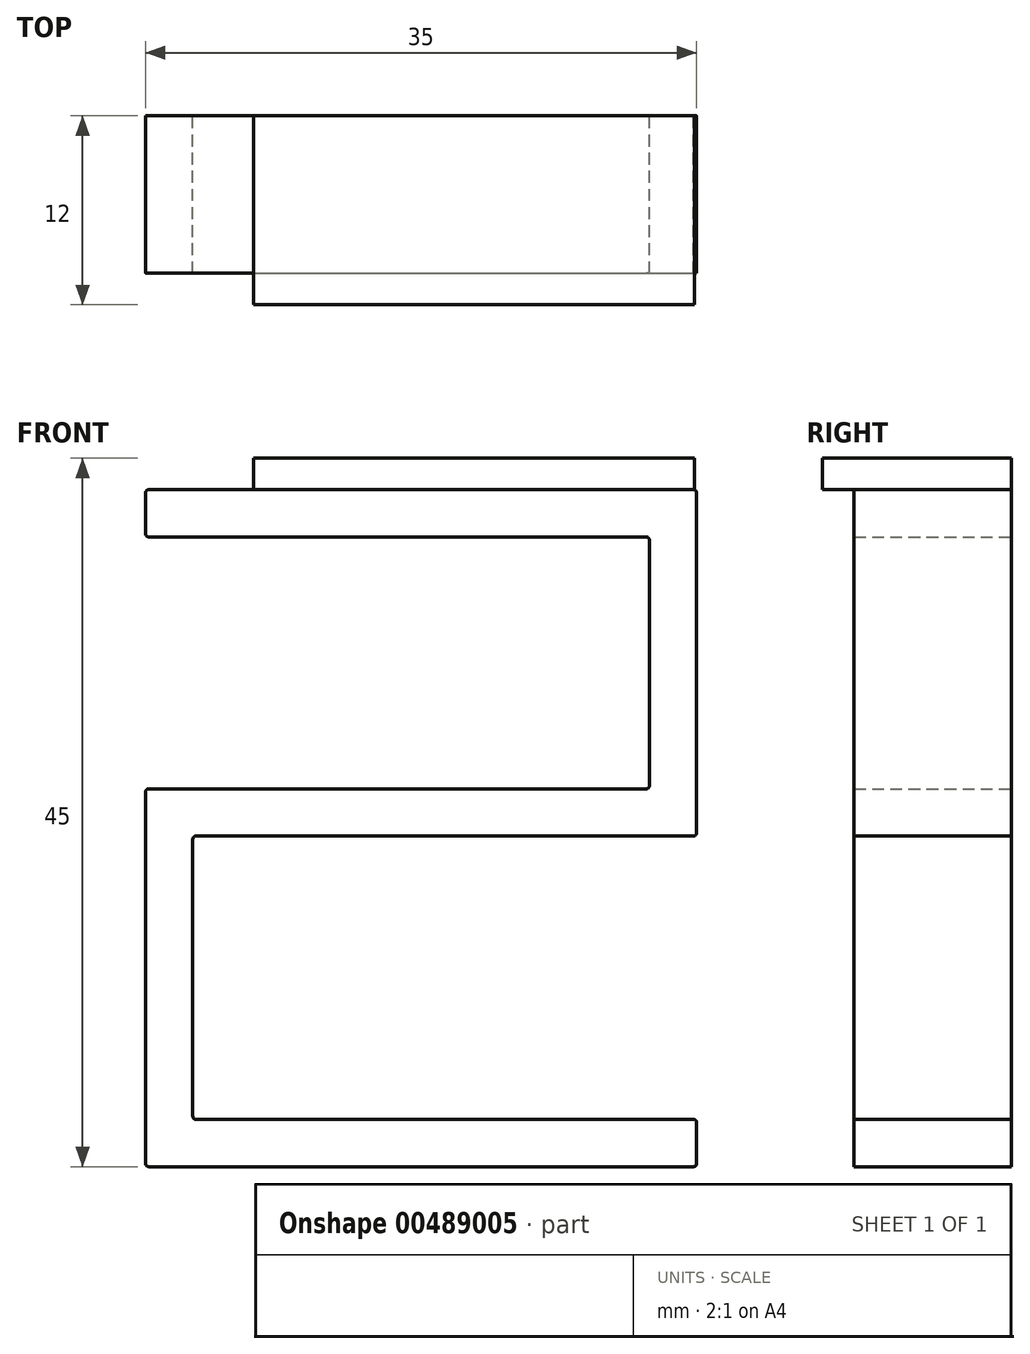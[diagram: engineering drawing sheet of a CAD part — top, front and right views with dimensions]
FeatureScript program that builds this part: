
annotation { "Feature Type Name" : "Feature", "Feature Type Description" : "" }
export const myFeature = defineFeature(function(context is Context, id is Id, definition is map)
    precondition{}
    {
        {
            var Q0;
            Q0=qCreatedBy(makeId("Front.planeOp"),FACE);
            var sketch = newSketch(context, id + "F0", { "sketchPlane" : qUnion([Q0])});
            skLineSegment(sketch, "E0.bottom", {"start": v(0, 0) * mm, "end": v(35, 0) * mm});
            skLineSegment(sketch, "E0.top", {"start": v(0, -43) * mm, "end": v(35, -43) * mm});
            skLineSegment(sketch, "E0.left", {"start": v(0, 0) * mm, "end": v(0, -3) * mm});
            skLineSegment(sketch, "E0.right", {"start": v(35, 0) * mm, "end": v(35, -22) * mm});
            skLineSegment(sketch, "E1.0", {"start": v(3, -40) * mm, "end": v(35, -40) * mm});
            skLineSegment(sketch, "E2.0", {"start": v(3, -22) * mm, "end": v(35, -22) * mm});
            skLineSegment(sketch, "E3.0", {"start": v(0, -19) * mm, "end": v(32, -19) * mm});
            skLineSegment(sketch, "E4.0", {"start": v(0, -3) * mm, "end": v(32, -3) * mm});
            skLineSegment(sketch, "E5.trimOffspring", {"start": v(3, -22) * mm, "end": v(3, -40) * mm});
            skLineSegment(sketch, "E6.trimOffspring", {"start": v(0, -19) * mm, "end": v(0, -43) * mm});
            skLineSegment(sketch, "E7.trimOffspring", {"start": v(32, -19) * mm, "end": v(32, -3) * mm});
            skLineSegment(sketch, "E8.trimOffspring", {"start": v(35, -40) * mm, "end": v(35, -43) * mm});
            skPoint(sketch, "E9.orphan", {"position": v(32, 0) * mm});
            skSolve(sketch);
        }
        {
            var Q0;
            Q0=makeQuery(id+"F0.imprint","IMPRINT",FACE,{"disambiguationData":[TD([[makeQuery(id+"F0.imprint","IMPRINT",EDGE,{"derivedFrom":sQuery(id+"F0.wireOp",EDGE,"E0.bottom")}),-1.0]])]});
            extrude(context, id + "F1", {"entities" : qUnion([Q0]), "depth" : 10 * mm, "offsetDistance" : 25 * mm});
        }
        {
            var Q0;
            Q0=makeQuery(id+"F1.opExtrude","SWEPT_EDGE",EDGE,{"disambiguationData":[OSD([sQuery(id+"F0.wireOp",EDGE,"E0.bottom"),sQuery(id+"F0.wireOp",EDGE,"E0.right")])]});
            var Q1;
            Q1=makeQuery(id+"F1.opExtrude","SWEPT_EDGE",EDGE,{"disambiguationData":[OSD([sQuery(id+"F0.wireOp",EDGE,"E4.0"),sQuery(id+"F0.wireOp",EDGE,"E7.trimOffspring")])]});
            var Q2;
            Q2=makeQuery(id+"F1.opExtrude","SWEPT_EDGE",EDGE,{"disambiguationData":[OSD([sQuery(id+"F0.wireOp",EDGE,"E0.right"),sQuery(id+"F0.wireOp",EDGE,"E2.0")])]});
            var Q3;
            Q3=makeQuery(id+"F1.opExtrude","SWEPT_EDGE",EDGE,{"disambiguationData":[OSD([sQuery(id+"F0.wireOp",EDGE,"E3.0"),sQuery(id+"F0.wireOp",EDGE,"E7.trimOffspring")])]});
            fillet(context, id + "F2", {"entities" : qUnion([Q0, Q1, Q2, Q3]), "radius" : 0.2 * mm, "tangentPropagation" : true, "allowEdgeOverflow" : false});
        }
        {
            var Q0;
            Q0=makeQuery(id+"F1.opExtrude","SWEPT_EDGE",EDGE,{"disambiguationData":[OSD([sQuery(id+"F0.wireOp",EDGE,"E1.0"),sQuery(id+"F0.wireOp",EDGE,"E5.trimOffspring")])]});
            var Q1;
            Q1=makeQuery(id+"F1.opExtrude","SWEPT_EDGE",EDGE,{"disambiguationData":[OSD([sQuery(id+"F0.wireOp",EDGE,"E1.0"),sQuery(id+"F0.wireOp",EDGE,"E8.trimOffspring")])]});
            var Q2;
            Q2=makeQuery(id+"F1.opExtrude","SWEPT_EDGE",EDGE,{"disambiguationData":[OSD([sQuery(id+"F0.wireOp",EDGE,"E0.top"),sQuery(id+"F0.wireOp",EDGE,"E8.trimOffspring")])]});
            var Q3;
            Q3=makeQuery(id+"F1.opExtrude","SWEPT_EDGE",EDGE,{"disambiguationData":[OSD([sQuery(id+"F0.wireOp",EDGE,"E0.top"),sQuery(id+"F0.wireOp",EDGE,"E6.trimOffspring")])]});
            var Q4;
            Q4=makeQuery(id+"F1.opExtrude","SWEPT_EDGE",EDGE,{"disambiguationData":[OSD([sQuery(id+"F0.wireOp",EDGE,"E2.0"),sQuery(id+"F0.wireOp",EDGE,"E5.trimOffspring")])]});
            var Q5;
            Q5=makeQuery(id+"F1.opExtrude","SWEPT_EDGE",EDGE,{"disambiguationData":[OSD([sQuery(id+"F0.wireOp",EDGE,"E3.0"),sQuery(id+"F0.wireOp",EDGE,"E6.trimOffspring")])]});
            var Q6;
            Q6=makeQuery(id+"F1.opExtrude","SWEPT_EDGE",EDGE,{"disambiguationData":[OSD([sQuery(id+"F0.wireOp",EDGE,"E0.bottom"),sQuery(id+"F0.wireOp",EDGE,"E0.left")])]});
            var Q7;
            Q7=makeQuery(id+"F1.opExtrude","SWEPT_EDGE",EDGE,{"disambiguationData":[OSD([sQuery(id+"F0.wireOp",EDGE,"E0.left"),sQuery(id+"F0.wireOp",EDGE,"E4.0")])]});
            fillet(context, id + "F3", {"entities" : qUnion([Q0, Q1, Q2, Q3, Q4, Q5, Q6, Q7]), "radius" : 0.2 * mm, "tangentPropagation" : true, "allowEdgeOverflow" : false});
        }
        {
            var Q0;
            Q0=qCreatedBy(makeId("Front.planeOp"),FACE);
            var sketch = newSketch(context, id + "F4", { "sketchPlane" : qUnion([Q0])});
            skLineSegment(sketch, "E10.bottom", {"start": v(34.86, 0) * mm, "end": v(6.86, 0) * mm});
            skLineSegment(sketch, "E10.top", {"start": v(34.86, 2) * mm, "end": v(6.86, 2) * mm});
            skLineSegment(sketch, "E10.left", {"start": v(34.86, 0) * mm, "end": v(34.86, 2) * mm});
            skLineSegment(sketch, "E10.right", {"start": v(6.86, 0) * mm, "end": v(6.86, 2) * mm});
            skSolve(sketch);
        }
        {
            var Q0;
            Q0=makeQuery(id+"F4.imprint","IMPRINT",FACE,{"disambiguationData":[TD([[makeQuery(id+"F4.imprint","IMPRINT",EDGE,{"derivedFrom":sQuery(id+"F4.wireOp",EDGE,"E10.bottom")}),-1.0]])]});
            extrude(context, id + "F5", {"entities" : qUnion([Q0]), "operationType" : NewBodyOperationType.ADD, "depth" : 25 * mm, "offsetDistance" : 25 * mm});
        }
        {
            var Q0;
            Q0=makeQuery(id+"F5.opExtrude","CAP_FACE",FACE,{"disambiguationData":[OSD([sQuery(id+"F4.wireOp",EDGE,"E10.bottom"),sQuery(id+"F4.wireOp",EDGE,"E10.top"),sQuery(id+"F4.wireOp",EDGE,"E10.left"),sQuery(id+"F4.wireOp",EDGE,"E10.right")])],"isStart":false});
            extrude(context, id + "F6", {"entities" : qUnion([Q0]), "operationType" : NewBodyOperationType.ADD, "oppositeDirection" : true, "depth" : 13 * mm, "offsetDistance" : 25 * mm});
        }
        {
            var Q0;
            Q0=makeQuery(id+"F5.opExtrude","CAP_FACE",FACE,{"disambiguationData":[OSD([sQuery(id+"F4.wireOp",EDGE,"E10.bottom"),sQuery(id+"F4.wireOp",EDGE,"E10.top"),sQuery(id+"F4.wireOp",EDGE,"E10.left"),sQuery(id+"F4.wireOp",EDGE,"E10.right")])],"isStart":false});
            extrude(context, id + "F7", {"entities" : qUnion([Q0]), "operationType" : NewBodyOperationType.REMOVE, "oppositeDirection" : true, "depth" : 12 * mm, "offsetDistance" : 25 * mm});
        }
        {
            var Q0;
            Q0=makeQuery(id+"F7.boolean.opBoolean","COPY",FACE,{"derivedFrom":makeQuery(id+"F7.opExtrude","CAP_FACE",FACE,{"disambiguationData":[OSD([sQuery(id+"F4.wireOp",EDGE,"E10.bottom"),sQuery(id+"F4.wireOp",EDGE,"E10.top"),sQuery(id+"F4.wireOp",EDGE,"E10.left"),sQuery(id+"F4.wireOp",EDGE,"E10.right")])],"isStart":false})});
            extrude(context, id + "F8", {"entities" : qUnion([Q0]), "operationType" : NewBodyOperationType.REMOVE, "oppositeDirection" : true, "depth" : 1 * mm, "offsetDistance" : 25 * mm});
        }
    });
